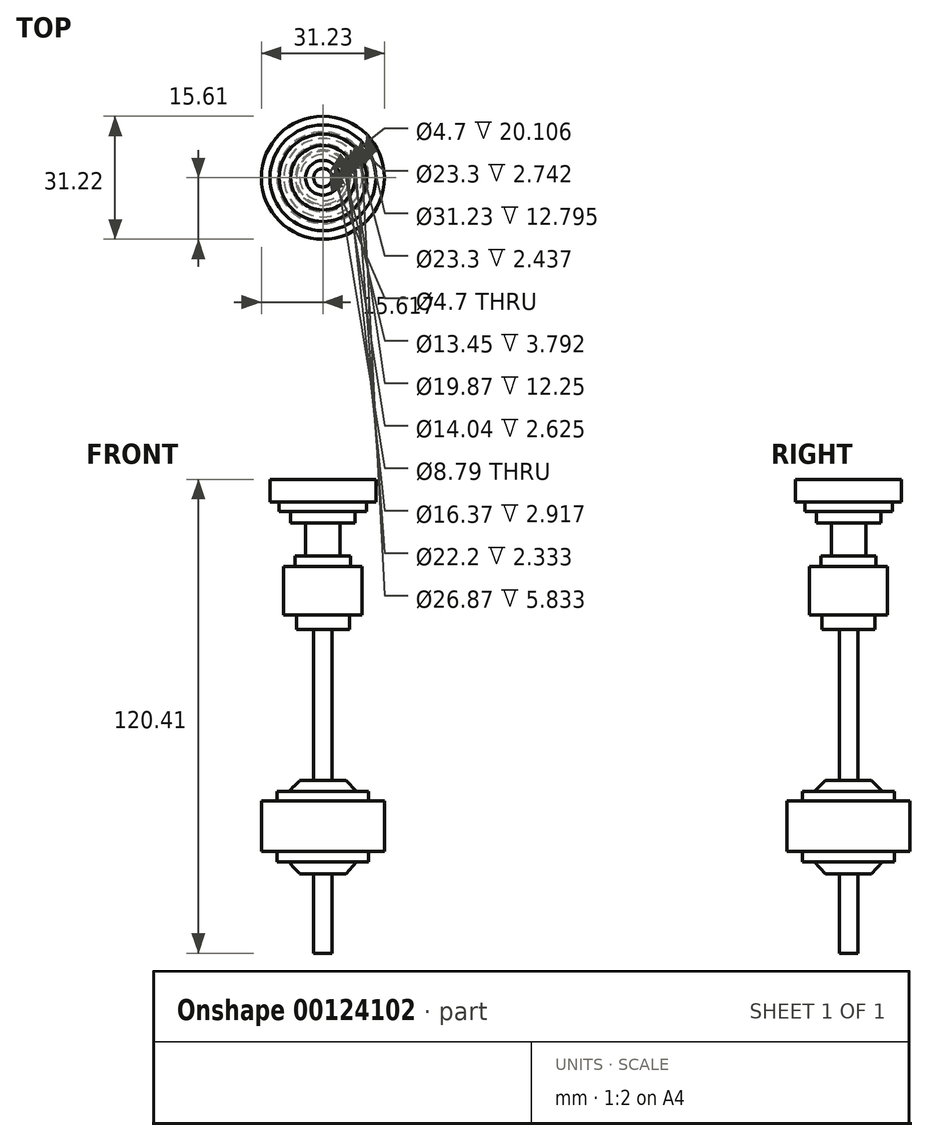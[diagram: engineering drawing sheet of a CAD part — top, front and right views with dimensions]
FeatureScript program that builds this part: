
annotation { "Feature Type Name" : "Feature", "Feature Type Description" : "" }
export const myFeature = defineFeature(function(context is Context, id is Id, definition is map)
    precondition{}
    {
        {
            var Q0;
            Q0=qCreatedBy(makeId("Front.planeOp"),FACE);
            var sketch = newSketch(context, id + "F0", { "sketchPlane" : qUnion([Q0])});
            skLineSegment(sketch, "E0", {"start": v(-59.2, 49.58) * mm, "end": v(-59.2, 43.75) * mm});
            skLineSegment(sketch, "E1", {"start": v(-59.2, 43.75) * mm, "end": v(-56.88, 43.75) * mm});
            skLineSegment(sketch, "E2", {"start": v(-56.88, 43.75) * mm, "end": v(-56.88, 41.42) * mm});
            skLineSegment(sketch, "E3", {"start": v(-56.88, 41.42) * mm, "end": v(-53.96, 41.42) * mm});
            skLineSegment(sketch, "E4", {"start": v(-53.96, 41.42) * mm, "end": v(-53.96, 38.5) * mm});
            skLineSegment(sketch, "E5", {"start": v(-53.96, 38.5) * mm, "end": v(-50.17, 38.5) * mm});
            skLineSegment(sketch, "E6", {"start": v(-50.17, 38.5) * mm, "end": v(-50.17, 30.04) * mm});
            skLineSegment(sketch, "E7", {"start": v(-50.17, 30.04) * mm, "end": v(-52.8, 30.04) * mm});
            skLineSegment(sketch, "E8", {"start": v(-52.8, 30.04) * mm, "end": v(-52.8, 27.42) * mm});
            skLineSegment(sketch, "E9", {"start": v(-52.8, 27.42) * mm, "end": v(-55.7, 27.42) * mm});
            skLineSegment(sketch, "E10", {"start": v(-55.7, 27.42) * mm, "end": v(-55.7, 15.17) * mm});
            skLineSegment(sketch, "E11", {"start": v(-55.7, 15.17) * mm, "end": v(-52.5, 15.17) * mm});
            skLineSegment(sketch, "E12", {"start": v(-52.5, 15.17) * mm, "end": v(-52.5, 11.38) * mm});
            skLineSegment(sketch, "E13", {"start": v(-52.5, 11.38) * mm, "end": v(-48.13, 11.38) * mm});
            skLineSegment(sketch, "E14", {"start": v(-48.13, 11.38) * mm, "end": v(-48.13, -26.96) * mm});
            skLineSegment(sketch, "E15", {"start": v(-48.13, -26.96) * mm, "end": v(-51.64, -26.96) * mm});
            skLineSegment(sketch, "E16", {"start": v(-51.64, -26.96) * mm, "end": v(-54.38, -29.7) * mm});
            skLineSegment(sketch, "E17", {"start": v(-54.38, -29.7) * mm, "end": v(-57.43, -29.7) * mm});
            skLineSegment(sketch, "E18", {"start": v(-57.43, -29.7) * mm, "end": v(-57.43, -32.14) * mm});
            skLineSegment(sketch, "E19", {"start": v(-57.43, -32.14) * mm, "end": v(-61.39, -32.14) * mm});
            skLineSegment(sketch, "E20", {"start": v(-61.39, -32.14) * mm, "end": v(-61.39, -44.93) * mm});
            skLineSegment(sketch, "E21", {"start": v(-61.39, -44.93) * mm, "end": v(-57.43, -44.93) * mm});
            skLineSegment(sketch, "E22", {"start": v(-57.43, -44.93) * mm, "end": v(-57.43, -47.68) * mm});
            skLineSegment(sketch, "E23", {"start": v(-57.43, -47.68) * mm, "end": v(-54.38, -47.68) * mm});
            skLineSegment(sketch, "E24", {"start": v(-54.38, -47.68) * mm, "end": v(-51.64, -50.72) * mm});
            skLineSegment(sketch, "E25", {"start": v(-51.64, -50.72) * mm, "end": v(-48.13, -50.72) * mm});
            skLineSegment(sketch, "E26", {"start": v(-48.13, -50.72) * mm, "end": v(-48.13, -70.83) * mm});
            skLineSegment(sketch, "E27", {"start": v(-45.77, 49.58) * mm, "end": v(-45.77, -70.83) * mm, "construction": true});
            skLineSegment(sketch, "E28", {"start": v(-59.2, 49.58) * mm, "end": v(-45.77, 49.58) * mm});
            skLineSegment(sketch, "E29", {"start": v(-45.77, -70.83) * mm, "end": v(-48.13, -70.83) * mm});
            skSolve(sketch);
        }
        {
            var Q0;
            Q0 = qSketchRegion(id + "F0", true);
            var Q1;
            Q1 = qConstructionFilter(qBodyType(qCreatedBy(id + "F0" ,EDGE), BodyType.WIRE), ConstructionObject.NO);
            var Q2;
            Q2=sQuery(id+"F0.wireOp",EDGE,"E27");
            revolve(context, id + "F1", {"bodyType" : ToolBodyType.SURFACE, "entities" : qUnion([Q0]), "surfaceEntities" : qUnion([Q1]), "axis" : qUnion([Q2]), "revolveType" : RevolveType.FULL});
        }
    });
